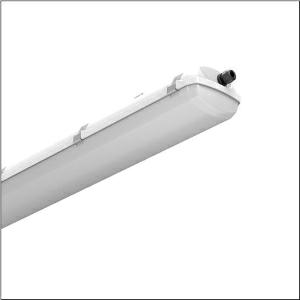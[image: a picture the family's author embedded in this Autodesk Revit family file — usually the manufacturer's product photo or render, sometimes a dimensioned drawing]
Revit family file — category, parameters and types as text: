
# Revit family: monsun_r__ex_51fxa27l460a_7d1b
name_source: partatom
category: Lighting Fixtures
units: mm (PartAtom-declared; Revit-internal decimal feet)

## family parameters
Cut with Voids When Loaded = No
Host = Face
Light Source = No
Part Type = Normal
Room Calculation Point = No
Round Connector Dimension = Use Diameter
Shared = No

## types (1)
- Monsun® Ex (1 x LED, 6560 lm, 53 W, 4000K)
    Apparent Load = 53 VA
    CIE Flux Codes = 46 76 94 98 100
    Color Rendering = 80
    Color Temperature = 4000K
    Default Elevation = 1800 mm
    Description = Monsun® Ex, damp-proof luminaire, primary optical cover: cover, of PC, UV-stabilised, opal, light emission: direct distribution, primary light characteristic: symmetric, installation type: surface-mounted, LED, rated luminous flux: 6.560lm, luminous efficacy: 124lm/W, light colour: 840, colour temperature: 4000K, control gear: ECG, with terminal, 3-pole, max. 2.5mm², through-wiring: 5x 2.5mm², mains connection: 220..250V, AC, 50/60Hz, rated input power: 53W, housing, of PC, light grey (RAL 7035), incl. 1x Ex cable gland M20 for cable diameter 7..12mm with sealing, incl. 1x Ex locking screw M20 with sealing, length: 1.280mm, width: 155mm, height: 105mm, clip for enclosure, of stainless steel, protection rating (complete): IP66, insulation class (complete): insulation class I (protective earthing), certification: CE, explosion class: zone 1,21 II 2G Ex eb mb op is IIC T4 Gb, II 2D Ex tb op is IIIC T67°C Db, impact resistance: IK10, permissible operating ambient temperature: -20..+40°C, contact your sales advisor before using the luminaires in applications with unclear chemical exposure, large temperature fluctuations or condensation-forming humidity, packaging unit: 1 piece
    Height = 105 mm
    Lamp = 1 x LED
    Lamp Light Flux = 6560 lm
    Lamp Power = 53 W
    Lamp count = 1
    Length = 1280 mm
    Luminous efficacy = 124 lm/W
    Manufacturer = Siteco
    ModVariant = No
    Model = 51FXA27L460A
    Mounting Place = Ceiling
    Mounting Type = Surface mounted
    Number of Poles = 1
    OnlyDefault = Yes
    Power Factor = 1
    Product Name = Monsun® Ex
    Product group = damp-proof luminaire
    ProductGroupID = 301
    Protection Class = Protection class I
    Protection Degree = IP 66
    RLX_Detail_Level = 1
    RLX_Emergency_Light_Flux = 0 lm
    RLX_Emergency_Type = 0
    RLX_Emergency_Type_DB = No
    RlxData = <blob elided: 41769 chars, md5=d567a4d8>
    Socket = socket
    Standby Power = 0 W
    System Light Flux = 6560 lm
    System Power = 53 W
    Type Comments = Product without accessories
    Type Image = l_1258882.jpg
    URL = http://relux.com
    VarID = ---
    Voltage = 0 V
    Weight = 0.00 kg
    Width = 155 mm

## geometry (parser evidence)
native form markers: Blend x4, Sweep x8
no freeform markers — native parametric forms only
